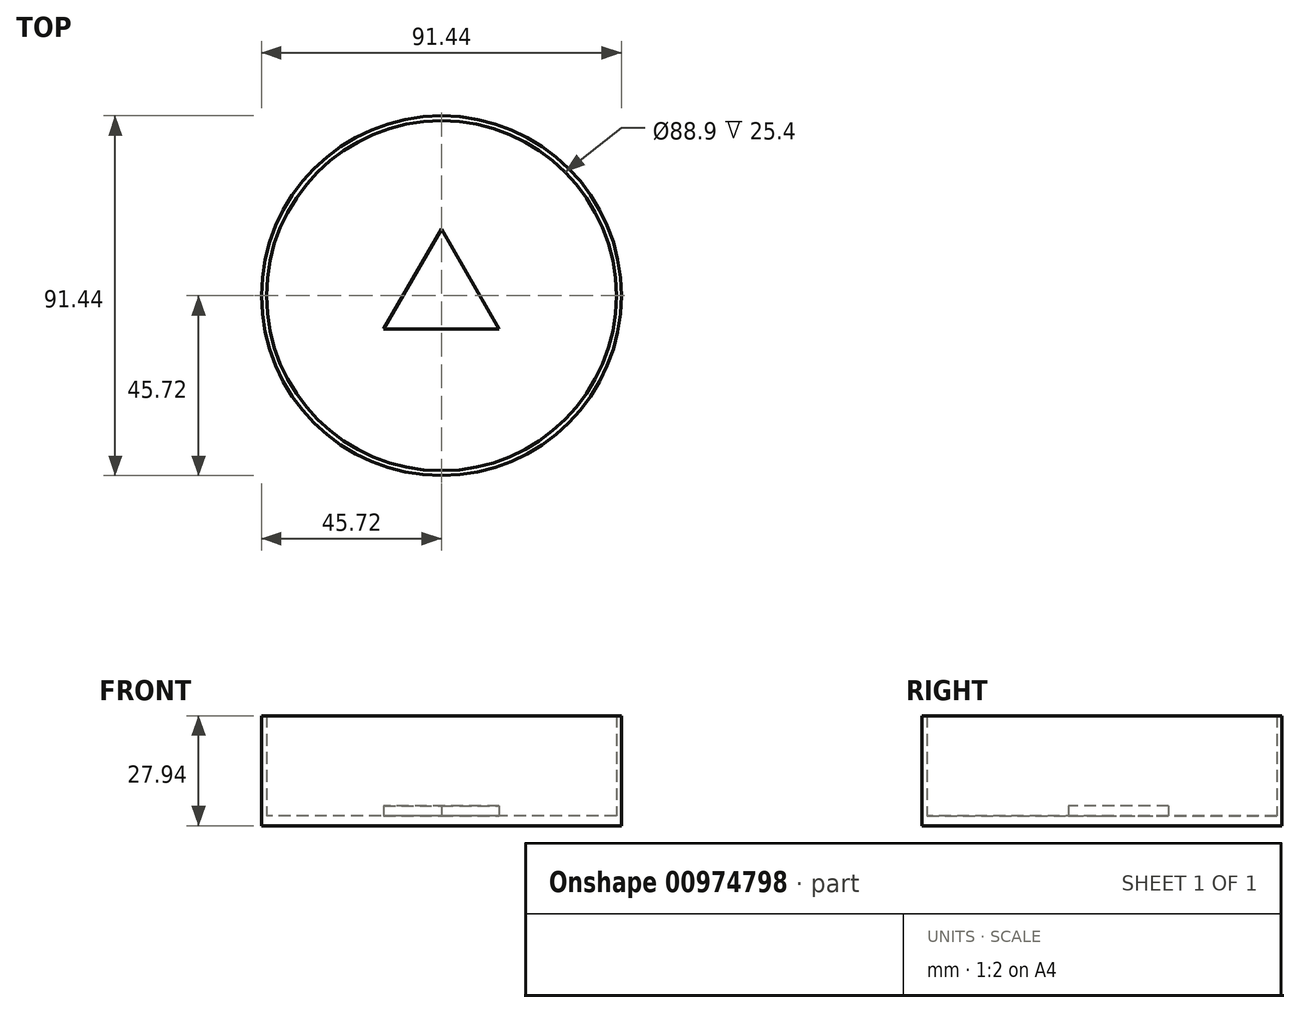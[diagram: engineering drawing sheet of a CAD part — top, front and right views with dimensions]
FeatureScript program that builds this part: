
annotation { "Feature Type Name" : "Feature", "Feature Type Description" : "" }
export const myFeature = defineFeature(function(context is Context, id is Id, definition is map)
    precondition{}
    {
        {
            var Q0;
            Q0=qCreatedBy(makeId("Top.planeOp"),FACE);
            var sketch = newSketch(context, id + "F0", { "sketchPlane" : qUnion([Q0])});
            skCircle(sketch, "E0", {"center": v(0, 0) * mm, "radius": 44.45 * mm});
            skCircle(sketch, "E1.0", {"center": v(0, 0) * mm, "radius": 45.72 * mm});
            skSolve(sketch);
        }
        {
            var Q0;
            Q0=makeQuery(id+"F0.imprint","IMPRINT",FACE,{"disambiguationData":[TD([[makeQuery(id+"F0.imprint","IMPRINT",EDGE,{"derivedFrom":sQuery(id+"F0.wireOp",EDGE,"E0")}),-1.0]])]});
            extrude(context, id + "F1", {"entities" : qUnion([Q0]), "depth" : 27.94 * mm, "offsetDistance" : 25.4 * mm});
        }
        {
            var Q0;
            Q0=makeQuery(id+"F0.imprint","IMPRINT",FACE,{"disambiguationData":[TD([[makeQuery(id+"F0.imprint","IMPRINT",EDGE,{"derivedFrom":sQuery(id+"F0.wireOp",EDGE,"E0")}),1.0]])]});
            extrude(context, id + "F2", {"entities" : qUnion([Q0]), "operationType" : NewBodyOperationType.ADD, "depth" : 2.54 * mm, "offsetDistance" : 25.4 * mm});
        }
        {
            var Q0;
            Q0=makeQuery(id+"F2.opExtrude","CAP_FACE",FACE,{"disambiguationData":[OSD([sQuery(id+"F0.wireOp",EDGE,"E0")])],"isStart":false});
            var sketch = newSketch(context, id + "F3", { "sketchPlane" : qUnion([Q0])});
            skCircle(sketch, "E2.cCircle", {"center": v(0, 0) * mm, "radius": 8.47 * mm, "construction": true});
            skLineSegment(sketch, "E2.0", {"start": v(14.66, -8.47) * mm, "end": v(-14.66, -8.47) * mm});
            skLineSegment(sketch, "E2.1", {"start": v(-14.66, -8.47) * mm, "end": v(0, 16.93) * mm});
            skLineSegment(sketch, "E2.2", {"start": v(0, 16.93) * mm, "end": v(14.66, -8.47) * mm});
            skPoint(sketch, "E2.0.midPoint", {"position": v(0, -8.47) * mm});
            skSolve(sketch);
        }
        {
            var Q0;
            Q0 = qSketchRegion(id + "F3", true);
            extrude(context, id + "F4", {"entities" : qUnion([Q0]), "operationType" : NewBodyOperationType.ADD, "depth" : 2.54 * mm, "offsetDistance" : 25.4 * mm});
        }
    });
